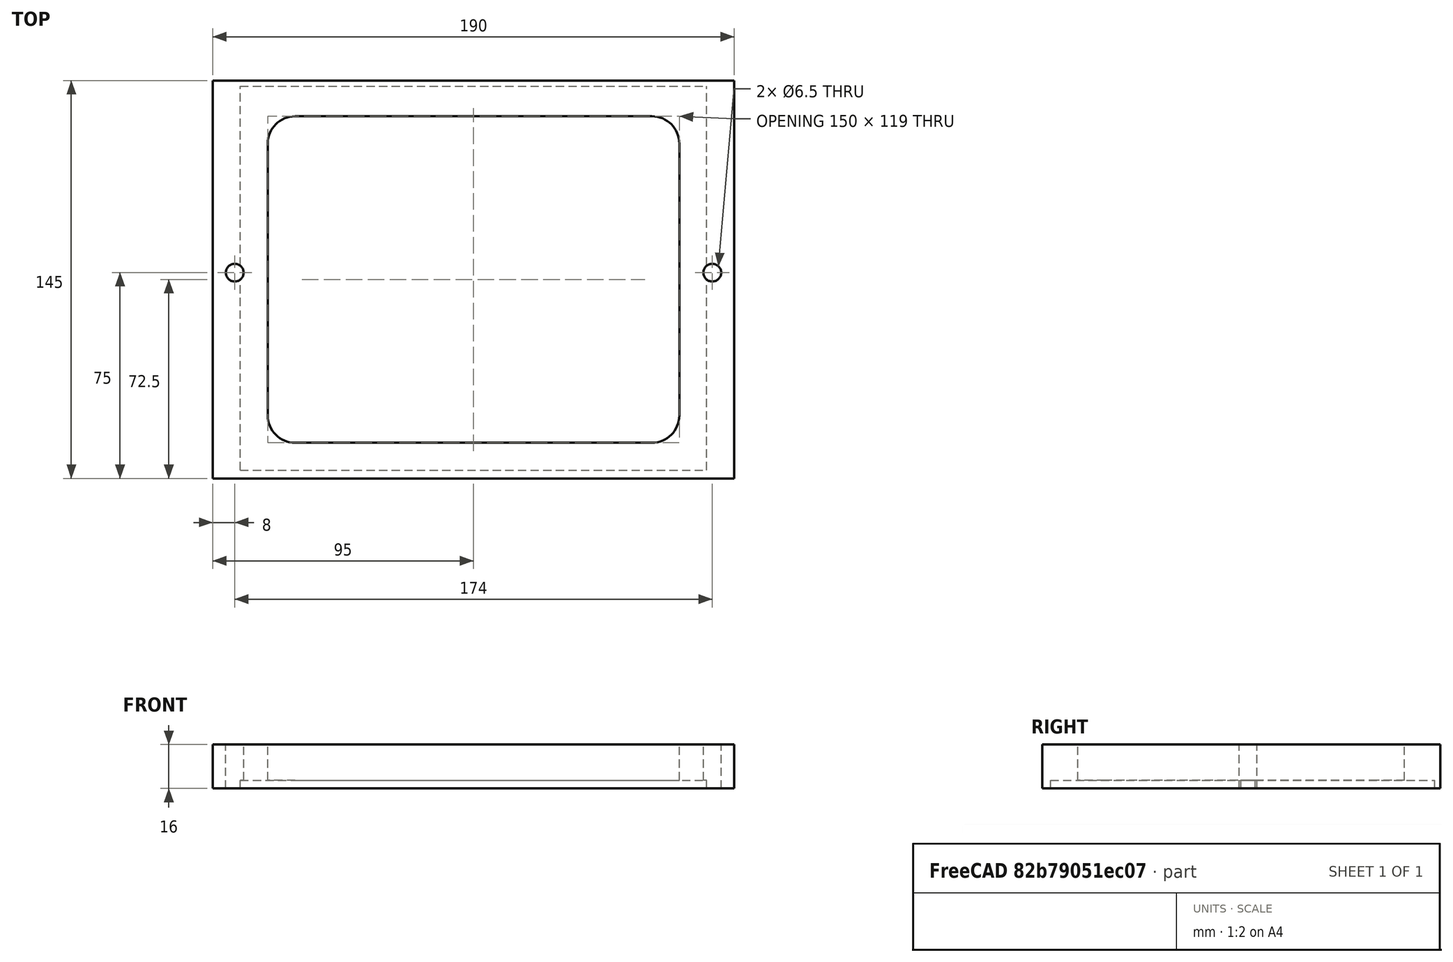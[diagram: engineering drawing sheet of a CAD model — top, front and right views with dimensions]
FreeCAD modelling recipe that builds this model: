
FCSTD DOCUMENT  (FreeCAD 0.15R4671 (Git))
Label: cubeta inferior sin tuerca
License: All rights reserved
LicenseURL: http://es.wikipedia.org/wiki/Todos_los_derechos_reservados
objects: Part::Box×3, Part::Cut×2, Part::Cylinder×1, Part::FeaturePython×1, Part::MultiFuse×1, Part::Fillet×1
note: 9 computed .brp shape members not serialized (recipe doc carries the construction recipe); baked Part::Feature solids carry a one-line shape summary decoded from their .brp

FEATURE [Part::Box] Box  label="Cubo"
  Height = 16
  Length = 190
  Width = 145
FEATURE [Part::Box] Box001  label="cristal"
  Height = 16
  Length = 150
  Placement = pos=(20,13,0) rot=(0,0,1;0rad)
  Width = 119
FEATURE [Part::Box] Box002  label="Cubo001"
  Height = 3
  Length = 170
  Placement = pos=(10,3,0) rot=(0,0,1;0rad)
  Width = 140
FEATURE [Part::Cylinder] Cylinder  label="Cilindro"
  Angle = 360
  Height = 26
  Placement = pos=(8,75,0) rot=(0,0,1;0rad)
  Radius = 3.25
FEATURE [Part::FeaturePython] Array  # Draft array (typed FeaturePython)
  Angle = 360
  ArrayType = 0
  Axis = (0,0,1)
  Base = -> Cylinder
  Center = (0,0,0)
  Fuse = false
  IntervalAxis = (0,0,0)
  IntervalX = (174,0,0)
  IntervalY = (0,1,0)
  IntervalZ = (0,0,0)
  NumberPolar = 2
  NumberX = 2
  NumberY = 1
  NumberZ = 1
FEATURE [Part::MultiFuse] Fusion
  Shapes = -> [Box001,Box002]
FEATURE [Part::Cut] Cut
  Base = -> Box
  Tool = -> Fusion
FEATURE [Part::Cut] Cut001
  Base = -> Cut
  Tool = -> Array
FEATURE [Part::Fillet] Fillet
  Base = -> Cut001
  Edges = 4 edges r=10: [Edge32,Edge34,Edge35,Edge37]
